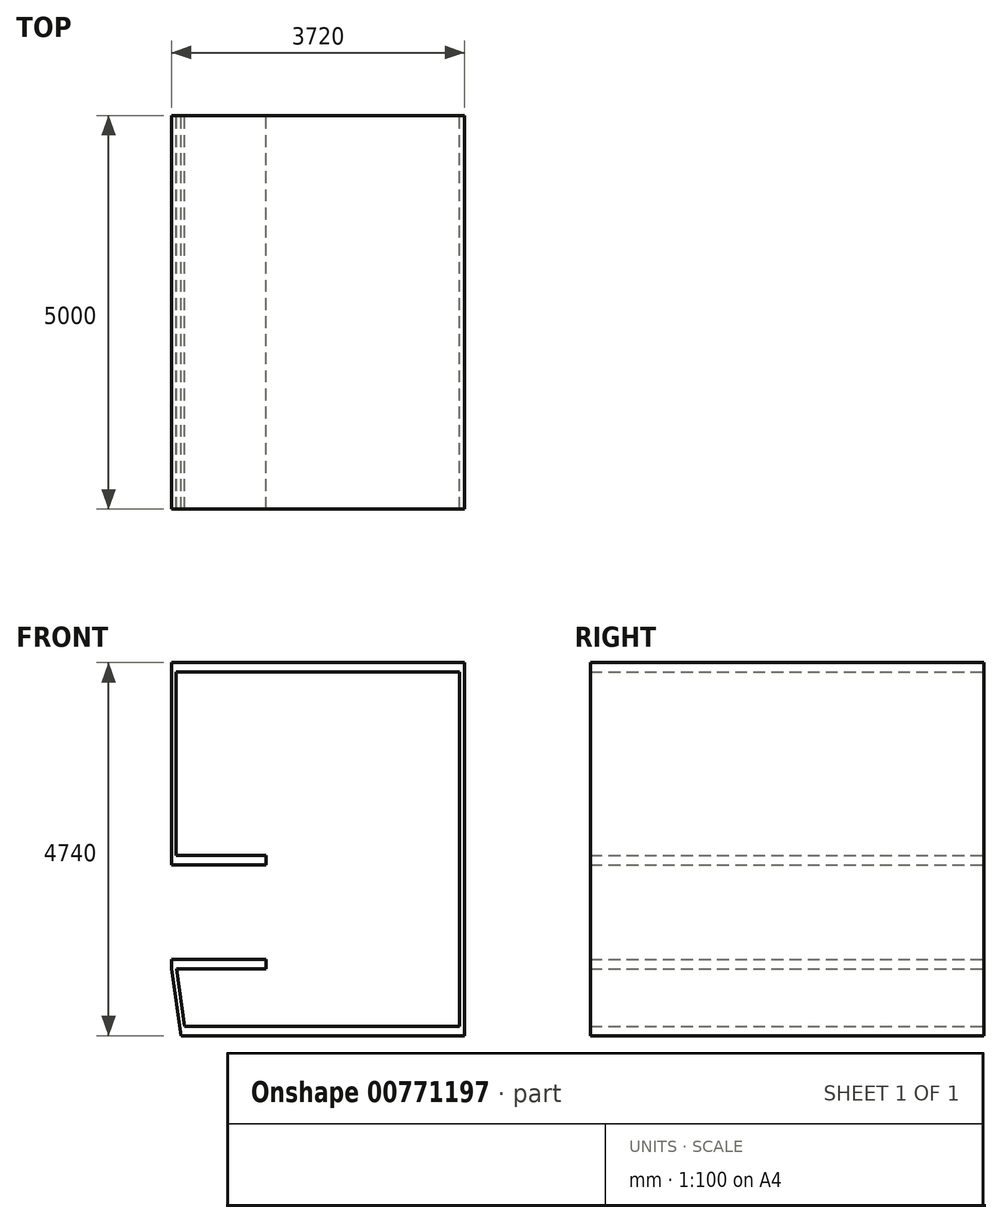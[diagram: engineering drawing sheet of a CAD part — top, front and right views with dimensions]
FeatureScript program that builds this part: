
annotation { "Feature Type Name" : "Feature", "Feature Type Description" : "" }
export const myFeature = defineFeature(function(context is Context, id is Id, definition is map)
    precondition{}
    {
        {
            var Q0;
            Q0=qCreatedBy(makeId("Front.planeOp"),FACE);
            var sketch = newSketch(context, id + "F0", { "sketchPlane" : qUnion([Q0])});
            skLineSegment(sketch, "E0.bottom", {"start": v(569.44, 532.23) * mm, "end": v(4169.44, 532.23) * mm});
            skLineSegment(sketch, "E0.top", {"start": v(449.44, 5272.23) * mm, "end": v(4169.44, 5272.23) * mm});
            skLineSegment(sketch, "E0.left", {"start": v(449.44, 1382.23) * mm, "end": v(449.44, 1502.23) * mm});
            skLineSegment(sketch, "E0.right", {"start": v(4169.44, 532.23) * mm, "end": v(4169.44, 5272.23) * mm});
            skLineSegment(sketch, "E1", {"start": v(449.44, 1382.23) * mm, "end": v(569.44, 532.23) * mm});
            skLineSegment(sketch, "E2", {"start": v(1649.44, 1502.23) * mm, "end": v(1649.44, 1382.23) * mm});
            skLineSegment(sketch, "E3", {"start": v(1649.44, 1382.23) * mm, "end": v(510.03, 1382.23) * mm});
            skLineSegment(sketch, "E4", {"start": v(510.03, 1382.23) * mm, "end": v(613.1, 652.23) * mm});
            skLineSegment(sketch, "E5", {"start": v(613.1, 652.23) * mm, "end": v(4109.44, 652.23) * mm});
            skLineSegment(sketch, "E6", {"start": v(4109.44, 652.23) * mm, "end": v(4109.44, 5152.23) * mm});
            skLineSegment(sketch, "E7", {"start": v(4109.44, 5152.23) * mm, "end": v(509.44, 5152.23) * mm});
            skLineSegment(sketch, "E8", {"start": v(509.44, 5152.23) * mm, "end": v(509.44, 2822.23) * mm});
            skLineSegment(sketch, "E9.top", {"start": v(509.44, 2822.23) * mm, "end": v(1649.44, 2822.23) * mm});
            skLineSegment(sketch, "E9.right", {"start": v(1649.44, 2702.23) * mm, "end": v(1649.44, 2822.23) * mm});
            skLineSegment(sketch, "E10", {"start": v(1649.44, 2702.23) * mm, "end": v(449.44, 2702.23) * mm});
            skPoint(sketch, "E11.start.orphan", {"position": v(509.44, 1502.23) * mm});
            skLineSegment(sketch, "E12", {"start": v(1649.44, 1502.23) * mm, "end": v(449.44, 1502.23) * mm});
            skLineSegment(sketch, "E13.trimOffspring", {"start": v(449.44, 2702.23) * mm, "end": v(449.44, 5272.23) * mm});
            skSolve(sketch);
        }
        {
            var Q0;
            Q0=makeQuery(id+"F0.imprint","IMPRINT",FACE,{"disambiguationData":[TD([[makeQuery(id+"F0.imprint","IMPRINT",EDGE,{"derivedFrom":sQuery(id+"F0.wireOp",EDGE,"E0.bottom")}),1.0]])]});
            extrude(context, id + "F1", {"entities" : qUnion([Q0]), "depth" : 5000 * mm, "offsetDistance" : 25 * mm});
        }
    });
